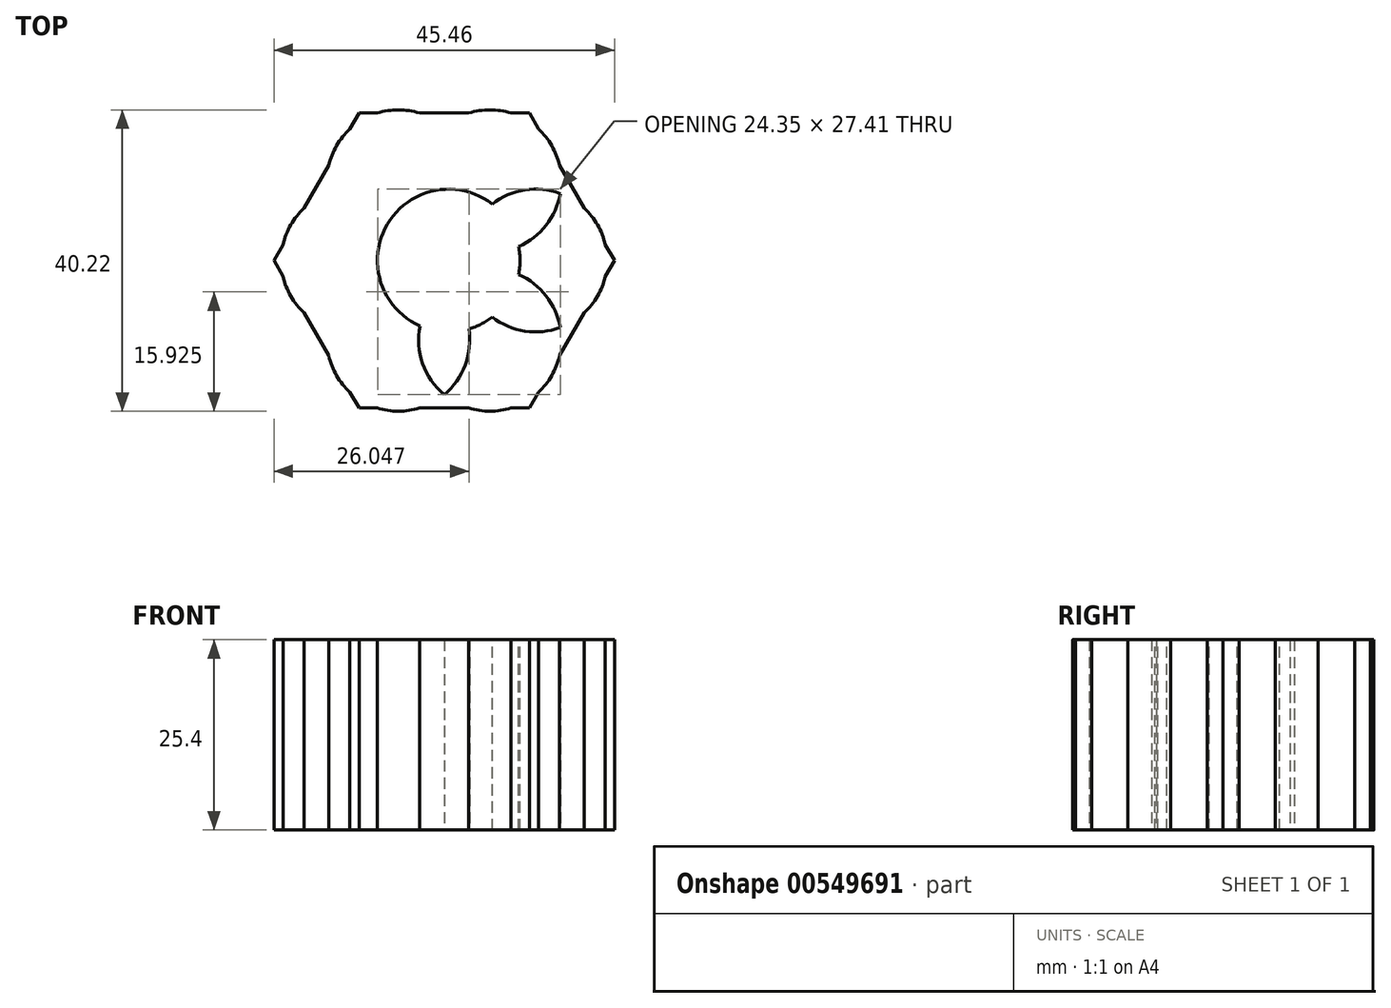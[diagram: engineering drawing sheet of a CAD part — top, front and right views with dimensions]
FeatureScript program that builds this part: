
annotation { "Feature Type Name" : "Feature", "Feature Type Description" : "" }
export const myFeature = defineFeature(function(context is Context, id is Id, definition is map)
    precondition{}
    {
        {
            var Q0;
            Q0=qCreatedBy(makeId("Top.planeOp"),FACE);
            var sketch = newSketch(context, id + "F0", { "sketchPlane" : qUnion([Q0])});
            skCircle(sketch, "E0.cCircle", {"center": v(0, 0) * mm, "radius": 13.34 * mm, "construction": true});
            skLineSegment(sketch, "E0.0", {"start": v(7.7, 13.33) * mm, "end": v(15.4, 0) * mm, "construction": true});
            skLineSegment(sketch, "E0.1", {"start": v(15.4, 0) * mm, "end": v(7.7, -13.33) * mm, "construction": true});
            skLineSegment(sketch, "E0.2", {"start": v(7.7, -13.33) * mm, "end": v(-7.7, -13.33) * mm, "construction": true});
            skLineSegment(sketch, "E0.3", {"start": v(-7.7, -13.33) * mm, "end": v(-15.4, 0) * mm, "construction": true});
            skLineSegment(sketch, "E0.4", {"start": v(-15.4, 0) * mm, "end": v(-7.7, 13.33) * mm, "construction": true});
            skLineSegment(sketch, "E0.5", {"start": v(-7.7, 13.33) * mm, "end": v(7.7, 13.33) * mm, "construction": true});
            skPoint(sketch, "E0.0.midPoint", {"position": v(11.55, 6.67) * mm});
            skCircle(sketch, "E1.cCircle", {"center": v(0, 0) * mm, "radius": 19.68 * mm, "construction": true});
            skLineSegment(sketch, "E1.0", {"start": v(-22.73, 0) * mm, "end": v(-11.37, 19.68) * mm});
            skLineSegment(sketch, "E1.1", {"start": v(-11.37, 19.68) * mm, "end": v(11.37, 19.68) * mm});
            skLineSegment(sketch, "E1.2", {"start": v(11.37, 19.68) * mm, "end": v(22.73, 0) * mm});
            skLineSegment(sketch, "E1.3", {"start": v(22.73, 0) * mm, "end": v(11.37, -19.68) * mm});
            skLineSegment(sketch, "E1.4", {"start": v(11.37, -19.68) * mm, "end": v(-11.37, -19.68) * mm});
            skLineSegment(sketch, "E1.5", {"start": v(-11.37, -19.68) * mm, "end": v(-22.73, 0) * mm});
            skPoint(sketch, "E1.0.midPoint", {"position": v(-17.05, 9.84) * mm});
            skCircle(sketch, "E2", {"center": v(-9.1, 4.56) * mm, "radius": 3.17 * mm, "construction": true});
            skCircle(sketch, "E3", {"center": v(-9.1, 4.56) * mm, "radius": 9.53 * mm, "construction": true});
            skLineSegment(sketch, "E4", {"start": v(-11.37, 19.68) * mm, "end": v(0, 0) * mm, "construction": true});
            skCircle(sketch, "E5", {"center": v(-6.11, 10.59) * mm, "radius": 3.17 * mm, "construction": true});
            skCircle(sketch, "E6", {"center": v(-6.11, 10.59) * mm, "radius": 9.53 * mm});
            skCircle(sketch, "E7.MirrorC", {"center": v(6.11, 10.59) * mm, "radius": 9.53 * mm});
            skCircle(sketch, "E8.MirrorC", {"center": v(-12.22, 0) * mm, "radius": 9.53 * mm});
            skCircle(sketch, "E9.MirrorC", {"center": v(-6.11, -10.59) * mm, "radius": 9.53 * mm});
            skCircle(sketch, "E10.MirrorC", {"center": v(6.11, -10.59) * mm, "radius": 9.53 * mm});
            skCircle(sketch, "E11.MirrorC", {"center": v(12.22, 0) * mm, "radius": 9.53 * mm});
            skSolve(sketch);
        }
        {
            var Q0;
            Q0 = qSketchRegion(id + "F0", true);
            var Q1;
            {var subQ0=sQuery(id+"F0.wireOp",EDGE,"E8.MirrorC");var subQ1=sQuery(id+"F0.wireOp",EDGE,"E6");var subQ2=makeQuery(id+"F0.imprint","INTERSECT",VERTEX,{"disambiguationData":[OD(0.0)],"derivedFrom":[subQ1,subQ0]});Q1=makeQuery(id+"F0.imprint","IMPRINT",FACE,{"disambiguationData":[TD([[makeQuery(id+"F0.imprint","IMPRINT",EDGE,{"disambiguationData":[TD([[subQ2,-1.0]])],"derivedFrom":subQ1}),1.0]])]});}
            var Q2;
            {var subQ0=sQuery(id+"F0.wireOp",EDGE,"E7.MirrorC");var subQ1=sQuery(id+"F0.wireOp",EDGE,"E6");var subQ2=makeQuery(id+"F0.imprint","INTERSECT",VERTEX,{"disambiguationData":[OD(0.0)],"derivedFrom":[subQ1,subQ0]});Q2=makeQuery(id+"F0.imprint","IMPRINT",FACE,{"disambiguationData":[TD([[makeQuery(id+"F0.imprint","IMPRINT",EDGE,{"disambiguationData":[TD([[subQ2,1.0]])],"derivedFrom":subQ1}),1.0]])]});}
            var Q3;
            Q3=makeQuery(id+"F0.imprint","IMPRINT",FACE,{"disambiguationData":[TD([[makeQuery(id+"F0.imprint","IMPRINT",EDGE,{"derivedFrom":sQuery(id+"F0.wireOp",EDGE,"E5")}),1.0]])]});
            var Q4;
            {var subQ0=sQuery(id+"F0.wireOp",EDGE,"E11.MirrorC");var subQ1=sQuery(id+"F0.wireOp",EDGE,"E7.MirrorC");var subQ2=makeQuery(id+"F0.imprint","INTERSECT",VERTEX,{"disambiguationData":[OD(0.0)],"derivedFrom":[subQ1,subQ0]});Q4=makeQuery(id+"F0.imprint","IMPRINT",FACE,{"disambiguationData":[TD([[makeQuery(id+"F0.imprint","IMPRINT",EDGE,{"disambiguationData":[TD([[subQ2,-1.0]])],"derivedFrom":subQ1}),-1.0]])]});}
            var Q5;
            {var subQ0=sQuery(id+"F0.wireOp",EDGE,"E11.MirrorC");var subQ1=sQuery(id+"F0.wireOp",EDGE,"E10.MirrorC");var subQ2=makeQuery(id+"F0.imprint","INTERSECT",VERTEX,{"disambiguationData":[OD(0.0)],"derivedFrom":[subQ1,subQ0]});Q5=makeQuery(id+"F0.imprint","IMPRINT",FACE,{"disambiguationData":[TD([[makeQuery(id+"F0.imprint","IMPRINT",EDGE,{"disambiguationData":[TD([[subQ2,-1.0]])],"derivedFrom":subQ1}),1.0]])]});}
            var Q6;
            {var subQ0=sQuery(id+"F0.wireOp",EDGE,"E10.MirrorC");var subQ1=sQuery(id+"F0.wireOp",EDGE,"E9.MirrorC");var subQ2=makeQuery(id+"F0.imprint","INTERSECT",VERTEX,{"disambiguationData":[OD(0.0)],"derivedFrom":[subQ1,subQ0]});Q6=makeQuery(id+"F0.imprint","IMPRINT",FACE,{"disambiguationData":[TD([[makeQuery(id+"F0.imprint","IMPRINT",EDGE,{"disambiguationData":[TD([[subQ2,1.0]])],"derivedFrom":subQ1}),-1.0]])]});}
            var Q7;
            {var subQ0=sQuery(id+"F0.wireOp",EDGE,"E9.MirrorC");var subQ1=sQuery(id+"F0.wireOp",EDGE,"E8.MirrorC");var subQ2=makeQuery(id+"F0.imprint","INTERSECT",VERTEX,{"disambiguationData":[OD(0.0)],"derivedFrom":[subQ1,subQ0]});Q7=makeQuery(id+"F0.imprint","IMPRINT",FACE,{"disambiguationData":[TD([[makeQuery(id+"F0.imprint","IMPRINT",EDGE,{"disambiguationData":[TD([[subQ2,-1.0]])],"derivedFrom":subQ1}),1.0]])]});}
            var Q8;
            {var subQ1=sQuery(id+"F0.wireOp",EDGE,"E8.MirrorC");var subQ5=sQuery(id+"F0.wireOp",EDGE,"E6");var subQ6=makeQuery(id+"F0.imprint","INTERSECT",VERTEX,{"disambiguationData":[OD(1.0)],"derivedFrom":[subQ5,subQ1]});Q8=makeQuery(id+"F0.imprint","IMPRINT",FACE,{"disambiguationData":[TD([[makeQuery(id+"F0.imprint","IMPRINT",EDGE,{"disambiguationData":[TD([[subQ6,-1.0]])],"derivedFrom":subQ5}),-1.0]])]});}
            extrude(context, id + "F1", {"entities" : qUnion([Q0, Q1, Q2, Q3, Q4, Q5, Q6, Q7, Q8]), "depth" : 25.4 * mm, "offsetDistance" : 25.4 * mm});
        }
        {
            var Q0;
            Q0=makeQuery(id+"F1.opExtrude","CAP_FACE",FACE,{"disambiguationData":[OSD([sQuery(id+"F0.wireOp",EDGE,"E1.0"),sQuery(id+"F0.wireOp",EDGE,"E1.1"),sQuery(id+"F0.wireOp",EDGE,"E1.2"),sQuery(id+"F0.wireOp",EDGE,"E1.3"),sQuery(id+"F0.wireOp",EDGE,"E1.4"),sQuery(id+"F0.wireOp",EDGE,"E1.5"),sQuery(id+"F0.wireOp",EDGE,"E6"),sQuery(id+"F0.wireOp",EDGE,"E7.MirrorC"),sQuery(id+"F0.wireOp",EDGE,"E8.MirrorC"),sQuery(id+"F0.wireOp",EDGE,"E9.MirrorC"),sQuery(id+"F0.wireOp",EDGE,"E10.MirrorC"),sQuery(id+"F0.wireOp",EDGE,"E11.MirrorC")])],"isStart":false});
            var sketch = newSketch(context, id + "F2", { "sketchPlane" : qUnion([Q0])});
            skCircle(sketch, "E12", {"center": v(0.6, 0) * mm, "radius": 9.53 * mm});
            skSolve(sketch);
        }
        {
            var Q0;
            Q0 = qSketchRegion(id + "F2", true);
            extrude(context, id + "F3", {"entities" : qUnion([Q0]), "operationType" : NewBodyOperationType.REMOVE, "endBound" : BoundingType.THROUGH_ALL, "oppositeDirection" : true, "depth" : 25.4 * mm, "offsetDistance" : 25.4 * mm});
        }
    });
